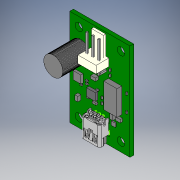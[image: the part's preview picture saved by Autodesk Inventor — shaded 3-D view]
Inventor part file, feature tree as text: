
AUTODESK INVENTOR PART (.ipt)
format: ipt  version: 2019 (Build 230136000, 136)  size: 742,912 bytes
history: native  units: in
note: dims shown in document units (in); Inventor stores cm internally (conversion verified against a paired STEP export)
features: extrude x29, sketch x7, other x5
ambient origin geometry x8: Origin, YZ Plane, XZ Plane, XY Plane, X Axis, Y Axis, Z Axis, Center Point
bodies: Solid1 (feature_tree), Solid2 (feature_tree), Solid3 (feature_tree), Solid4 (feature_tree), Solid5 (feature_tree), Solid6 (feature_tree), Solid7 (feature_tree), Solid8 (feature_tree), Solid9 (feature_tree), Solid10 (feature_tree), Solid11 (feature_tree), Solid12 (feature_tree), Solid13 (feature_tree), Solid14 (feature_tree), Solid15 (feature_tree), Solid16 (feature_tree), Solid17 (feature_tree), Solid18 (feature_tree), Solid19 (feature_tree), Solid20 (feature_tree), Solid21 (feature_tree), Solid22 (feature_tree), Solid23 (feature_tree), Solid24 (feature_tree), Solid25 (feature_tree), Solid26 (feature_tree), Solid27 (feature_tree), Solid28 (feature_tree), Solid29 (feature_tree), Solid30 (feature_tree), Solid31 (feature_tree), Solid32 (feature_tree), Solid33 (feature_tree)
feature tree (41):
  other  "Repaired Geometry1"
  sketch  "3D Sketch1"
  sketch  "3D Sketch2"
  sketch  "3D Sketch3"
  sketch  "3D Sketch4"
  sketch  "3D Sketch5"
  sketch  "3D Sketch6"
  sketch  "3D Sketch7"
  other  "Board_5896:1"
  extrude  "Extruded_5897:1"  [1 undecoded]
  extrude  "Extruded_5900:1"  [1 undecoded]
  extrude  "Extruded_5903:1"  [1 undecoded]
  extrude  "Extruded_5906:1"  [1 undecoded]
  other  "Open CASCADE STEP translator 6.2 252.6.1.1_5909:1"
  extrude  "Extruded_5913:1"  [1 undecoded]
  extrude  "Extruded_5900:2"  [1 undecoded]
  extrude  "Extruded_5918:1"  [1 undecoded]
  other  "Cylinder_5921:1"
  other  "Cylinder_5921:2"
  extrude  "Extruded_5924:1"  [1 undecoded]
  extrude  "Extruded_5900:3"  [1 undecoded]
  extrude  "Extruded_5929:1"  [1 undecoded]
  extrude  "Extruded_5931:1"  [1 undecoded]
  extrude  "Extruded_5933:1"  [1 undecoded]
  extrude  "Extruded_5933:2"  [1 undecoded]
  extrude  "Extruded_5933:3"  [1 undecoded]
  extrude  "Extruded_5937:1"  [1 undecoded]
  extrude  "Extruded_5937:2"  [1 undecoded]
  extrude  "Extruded_5937:3"  [1 undecoded]
  extrude  "Extruded_5942:1"  [1 undecoded]
  extrude  "Extruded_5945:1"  [1 undecoded]
  extrude  "Extruded_5897:2"  [1 undecoded]
  extrude  "Extruded_5900:4"  [1 undecoded]
  extrude  "Extruded_5900:5"  [1 undecoded]
  extrude  "Extruded_5954:1"  [1 undecoded]
  extrude  "Extruded_5900:6"  [1 undecoded]
  extrude  "Extruded_5959:1"  [1 undecoded]
  extrude  "Extruded_5962:1"  [1 undecoded]
  extrude  "Extruded_5897:3"  [1 undecoded]
  extrude  "Extruded_5897:4"  [1 undecoded]
  extrude  "Extruded_5897:5"  [1 undecoded]
note: 29 required parameter values undecoded (feature->parameter linkage not recoverable at this tier; creation-order binding heuristic only, values carry confidence <= 0.55)
